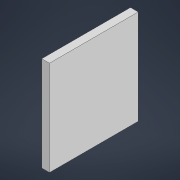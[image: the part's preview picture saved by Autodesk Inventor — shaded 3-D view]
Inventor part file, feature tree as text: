
AUTODESK INVENTOR PART (.ipt)
format: ipt  version: 2022 (Build 260153000, 153)  size: 85,504 bytes
history: native  units: mm
features: other x1, extrude x1, sketch x1
ambient origin geometry x8: Origin, YZ Plane, XZ Plane, XY Plane, X Axis, Y Axis, Z Axis, Center Point
bodies: Body1 (feature_tree)
feature tree (3):
  other  "Твердое тело1"
  extrude  "Выдавливание1"  Depth=270.0mm
  sketch  "Эскиз1"
